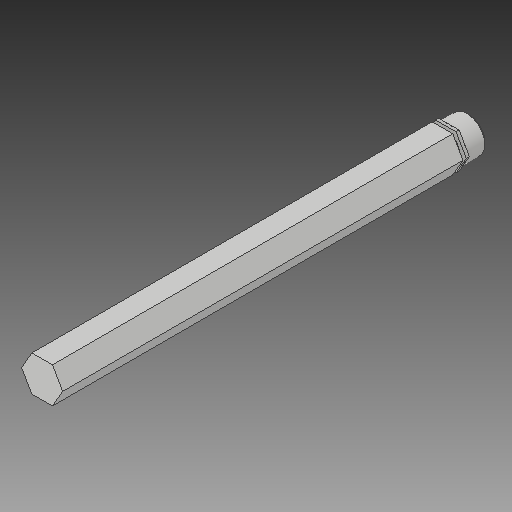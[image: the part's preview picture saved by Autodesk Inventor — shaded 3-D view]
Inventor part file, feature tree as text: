
AUTODESK INVENTOR PART (.ipt)
format: ipt  version: 2017 (Build 210142000, 142)  size: 87,552 bytes
history: native  units: in
note: dims shown in document units (in); Inventor stores cm internally (conversion verified against a paired STEP export)
features: chamfer x1
ambient origin geometry x8: Origin, YZ Plane, XZ Plane, XY Plane, X Axis, Y Axis, Z Axis, Center Point
bodies: Solid1 (feature_tree)
feature tree (1):
  chamfer  "Chamfer1"  [1 undecoded]
note: 1 required parameter value undecoded (feature->parameter linkage not recoverable at this tier; creation-order binding heuristic only, values carry confidence <= 0.55)
